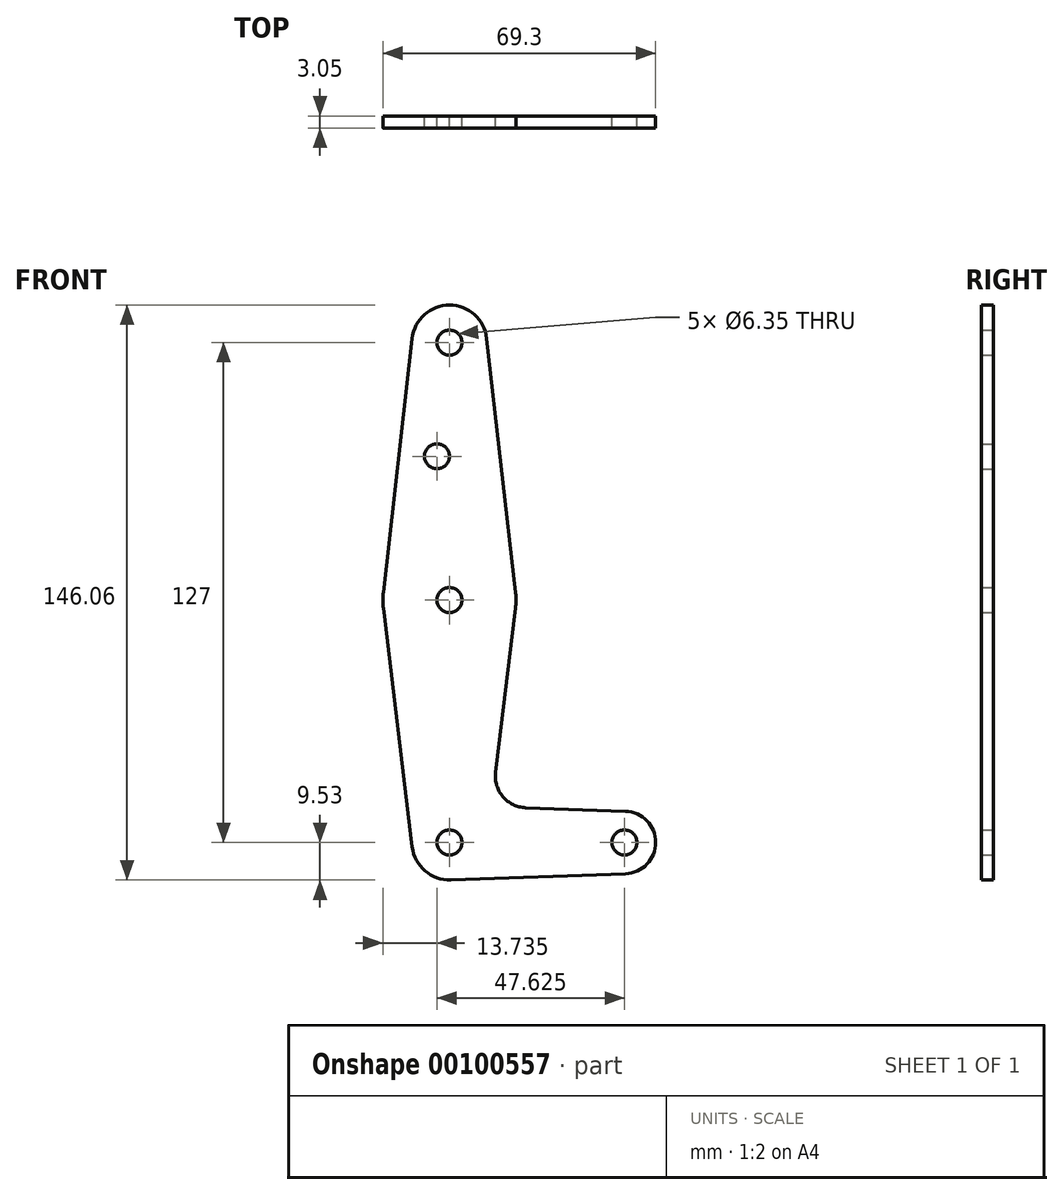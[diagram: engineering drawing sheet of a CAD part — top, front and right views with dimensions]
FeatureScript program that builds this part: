
annotation { "Feature Type Name" : "Feature", "Feature Type Description" : "" }
export const myFeature = defineFeature(function(context is Context, id is Id, definition is map)
    precondition{}
    {
        {
            var Q0;
            Q0=qCreatedBy(makeId("Front.planeOp"),FACE);
            var sketch = newSketch(context, id + "F0", { "sketchPlane" : qUnion([Q0])});
            skLineSegment(sketch, "E0", {"start": v(0, 63.5) * mm, "end": v(0, 0) * mm});
            skLineSegment(sketch, "E1", {"start": v(0, 0) * mm, "end": v(0, -63.5) * mm});
            skCircle(sketch, "E2", {"center": v(0, 63.5) * mm, "radius": 9.53 * mm});
            skCircle(sketch, "E3", {"center": v(0, -1.9) * mm, "radius": 16.91 * mm});
            skCircle(sketch, "E4", {"center": v(0, -63.5) * mm, "radius": 9.53 * mm});
            skLineSegment(sketch, "E5", {"start": v(16.8, 0) * mm, "end": v(9.46, 64.58) * mm});
            skLineSegment(sketch, "E6", {"start": v(-16.8, 0) * mm, "end": v(-9.46, 64.58) * mm});
            skLineSegment(sketch, "E7", {"start": v(-16.79, -3.94) * mm, "end": v(-9.46, -64.64) * mm});
            skCircle(sketch, "E8", {"center": v(0, -63.5) * mm, "radius": 3.18 * mm});
            skCircle(sketch, "E9", {"center": v(0, -1.9) * mm, "radius": 3.18 * mm});
            skCircle(sketch, "E10", {"center": v(0, 63.5) * mm, "radius": 3.18 * mm});
            skCircle(sketch, "E11", {"center": v(-3.17, 34.62) * mm, "radius": 3.18 * mm});
            skLineSegment(sketch, "E12", {"start": v(0, -63.5) * mm, "end": v(44.45, -63.5) * mm});
            skCircle(sketch, "E13", {"center": v(44.45, -63.5) * mm, "radius": 7.94 * mm});
            skLineSegment(sketch, "E14", {"start": v(16.79, -3.94) * mm, "end": v(11.74, -45.76) * mm});
            skLineSegment(sketch, "E15", {"start": v(19.35, -54.66) * mm, "end": v(44.73, -55.57) * mm});
            skLineSegment(sketch, "E16", {"start": v(0.34, -73.02) * mm, "end": v(44.73, -71.43) * mm});
            skCircle(sketch, "E17", {"center": v(44.45, -63.5) * mm, "radius": 3.18 * mm});
            skArc(sketch, "E18.filletArc", {"start": v(11.74, -45.76) * mm, "mid": v(13.59, -51.88) * mm, "end": v(19.35, -54.66) * mm});
            skSolve(sketch);
        }
        {
            var Q0;
            Q0 = qSketchRegion(id + "F0", true);
            var Q1;
            {var subQ0=sQuery(id+"F0.wireOp",EDGE,"E4");var subQ1=sQuery(id+"F0.wireOp",EDGE,"E1");var subQ2=makeQuery(id+"F0.imprint","INTERSECT",VERTEX,{"derivedFrom":[subQ1,subQ0]});Q1=makeQuery(id+"F0.imprint","IMPRINT",FACE,{"disambiguationData":[TD([[makeQuery(id+"F0.imprint","IMPRINT",EDGE,{"disambiguationData":[TD([[subQ2,-1.0]])],"derivedFrom":subQ1}),1.0]])]});}
            extrude(context, id + "F1", {"entities" : qUnion([Q0, Q1]), "depth" : 3.05 * mm});
        }
    });
